# Revit family: NELE201LE
name_source: partatom
category: Lighting Fixtures
revit_build: Autodesk Revit 2014 (Build: 20130308_1515(x64)
units: mm (PartAtom-declared; Revit-internal decimal feet)

## types (1)
- NELE/201/LE
    Apparent Load = 6 VA
    Assembly Code = D5020200
    Color Filter = 16777215
    Connector Description = Lighting Connector
    Default Elevation = 1219.2 mm  [stored 4 ft]
    Description = The NexLED bulkhead luminaire utilises high output 1 Watt light emitting diodes (LED's) that provide a white, instant light that is highly visible. Designed for low profile applications, the bulkhead can be mounted on walls, handrails and ceilings making it ideal for walkways or restricted height areas. Its excellent temperature range of -45°C to +55°C makes it a global lighting solution providing high quality lighting at extreme temperatures. Green LED option is also available.
    Dimming Lamp Color Temperature Shift = <None>
    Drum-Height = 609.6 mm  [stored 2 ft]
    Emit Shape Visible in Rendering = No
    Emit from Rectangle Length = 173 mm
    Emit from Rectangle Width = 280 mm
    Features = Installation to gas groups IIA, IIB and IIC.
Highly visible, instant light.
Easy to install and maintain.
Ultra long life, no re-lamping required.
Over 60,000 hours* continuous operation.
Very low power consumption.
Highly Energy Efficient.
    Fixture distribution = Direct
    Housing Material = Paint - Hubbell - Textured Camera Black
    IP Rating = IP66/67
    Lamp = LED
    Length = 300 mm
    Load Classification = Lighting
    Manufacturer = Chalmit
    Model = NELE/201/LE
    Mounting = Paint - Hubbell - Light Silver
    Photometric Web File = NELE_201_LE.ies
    Power Factor = 1
    Product Documentation Link = https://hubbellcdn.com
    Product Link = https://www.hubbell.com
    Reflector Finish = Hubbell - White Glass
    Tilt Angle = 90.00°
    URL = https://www.hubbell.com
    Voltage = 120 V
    Warranty = 5 years Warranty
    Wattage Comments = 6W
    Watts = 6 W
    Width = 193 mm  [stored 0.633202 ft]
    Wings = Paint - Hubbell - Light Silver

note: [stored X ft] marks values corroborated as IEEE doubles in the binary element streams (Revit-internal decimal feet)

## geometry (parser evidence)
native form markers: Sweep x3
no freeform markers — native parametric forms only
